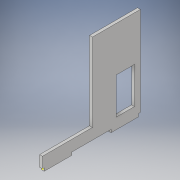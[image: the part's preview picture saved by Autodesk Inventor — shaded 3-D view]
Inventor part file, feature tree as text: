
AUTODESK INVENTOR PART (.ipt)
format: ipt  version: 2019 (Build 230136000, 136)  size: 128,512 bytes
history: native  units: in
note: dims shown in document units (in); Inventor stores cm internally (conversion verified against a paired STEP export)
features: sketch x4, extrude x3
ambient origin geometry x8: Origin, YZ Plane, XZ Plane, XY Plane, X Axis, Y Axis, Z Axis, Center Point
bodies: Solid1 (feature_tree)
feature tree (7):
  extrude  "Extrusion1"  Depth=0.125in
  extrude  "Extrusion2"  Depth=1.2in
  sketch  "Sketch3"  dims[d4=1.2in d5=0.075in]
  extrude  "Extrusion3"  Depth=0.075in
  sketch  "Sketch1"  dims[d0=4.25in d1=0.125in]
  sketch  "Sketch2"  dims[d2=0.125in d3=1.2in]
  sketch  "Sketch4"  dims[d6=0.075in d7=3.875in d8=0.125in d9=0.0in d10=1.585in d11=0.8in d12=0.35in d14=0.25in d15=0.125in d16=0.0in d17=0.125in d18=0.0in]
